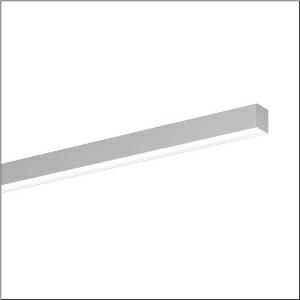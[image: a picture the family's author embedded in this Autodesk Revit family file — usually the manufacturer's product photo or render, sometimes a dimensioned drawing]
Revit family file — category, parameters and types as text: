
# Revit family: silica_r__21_51mx23db45sb_b235
name_source: partatom
category: Lighting Fixtures
units: mm (PartAtom-declared; Revit-internal decimal feet)

## family parameters
Cut with Voids When Loaded = No
Host = Face
Light Source = No
Part Type = Normal
Room Calculation Point = No
Round Connector Dimension = Use Diameter
Shared = No

## types (1)
- --- (1 x LED, 4100 lm, 28.1 W, 4000K)
    Apparent Load = 28 VA
    CIE Flux Codes = 78 96 99 100 100
    Color Rendering = 80
    Color Temperature = 4000K
    Default Elevation = 1800 mm
    Description = Silica® 21, office luminaire, primary optical cover: prismatic diffuser, of PMMA, CAT 2 (L<= 3000cd/m²), light emission: direct distribution, primary light characteristic: symmetric, installation type: surface-mounted, LED, rated luminous flux: 4.100lm, luminous efficacy: 146lm/W, light colour: 840, colour temperature: 4000K, control gear: DALI 2, with terminal, 3+2-pole, max. 2.5mm², mains connection: 220..240V, AC, 50/60Hz, rated input power: 28.1W, luminaire housing, of aluminium, metallic grey (RAL 9006), length: 1.504mm, width: 53mm, height: 53mm, protection rating (complete): IP20, insulation class (complete): insulation class I (protective earthing), certification: CE, permissible operating ambient temperature: 0..+35°C, standard: EN 50419, packaging unit: 1 piece
    Height = 53 mm
    Lamp = 1 x LED
    Lamp Light Flux = 4100 lm
    Lamp Power = 28.1 W
    Lamp count = 1
    Length = 1504 mm
    Luminous efficacy = 146 lm/W
    Manufacturer = Siteco
    ModVariant = No
    Model = 51MX23DB45SB
    Mounting Place = Ceiling
    Mounting Type = Surface mounted
    Number of Poles = 1
    OnlyDefault = Yes
    Power Factor = 1
    Product Name = Silica® 21
    Product group = office luminaire | ceiling mounted
    ProductGroupID = 302
    Protection Class = Protection class I
    Protection Degree = IP 20
    RLX_Detail_Level = 1
    RLX_Emergency_Light_Flux = 0 lm
    RLX_Emergency_Type = 0
    RLX_Emergency_Type_DB = No
    RlxData = <blob elided: 21333 chars, md5=fe1deb55>
    Socket = socket
    Standby Power = 0 W
    System Light Flux = 4100 lm
    System Power = 28 W
    Type Comments = factory setting: luminous flux: 100 % | dim-lin: 254 | 323 mA
    Type Image = l_1335933.jpg
    URL = http://relux.com
    VarID = @adj_119254
    Voltage = 0 V
    Weight = 0.00 kg
    Width = 53 mm

## geometry (parser evidence)
native form markers: Blend x4, Sweep x10
no freeform markers — native parametric forms only
